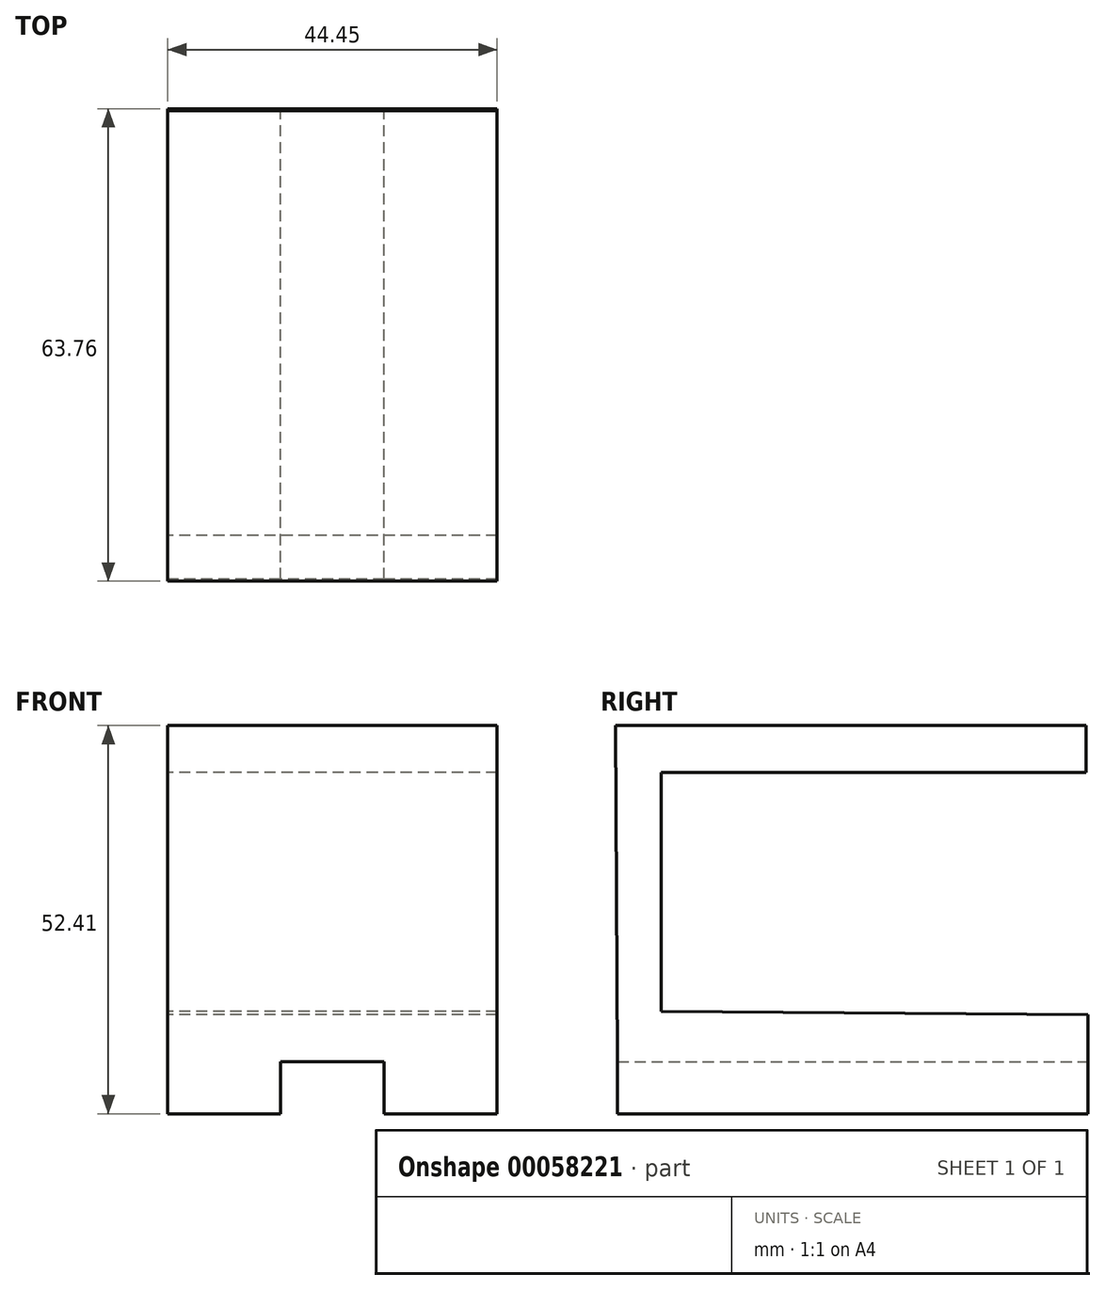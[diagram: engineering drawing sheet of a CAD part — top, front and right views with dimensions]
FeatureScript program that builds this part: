
annotation { "Feature Type Name" : "Feature", "Feature Type Description" : "" }
export const myFeature = defineFeature(function(context is Context, id is Id, definition is map)
    precondition{}
    {
        {
            var Q0;
            Q0=qCreatedBy(makeId("Right.planeOp"),FACE);
            var sketch = newSketch(context, id + "F0", { "sketchPlane" : qUnion([Q0])});
            skLineSegment(sketch, "E0.rect.bottom", {"start": v(31.75, -3.17) * mm, "end": v(-25.59, -3.17) * mm});
            skLineSegment(sketch, "E0.rect.top", {"start": v(31.75, 3.18) * mm, "end": v(-31.75, 3.18) * mm});
            skLineSegment(sketch, "E0.rect.left", {"start": v(31.75, -3.17) * mm, "end": v(31.75, 3.18) * mm});
            skPoint(sketch, "E0.rect.middle", {"position": v(0, 0) * mm});
            skLineSegment(sketch, "E1", {"start": v(-25.59, -3.17) * mm, "end": v(-25.59, -3.17) * mm});
            skLineSegment(sketch, "E2", {"start": v(-25.59, -3.17) * mm, "end": v(-25.59, -35.43) * mm});
            skLineSegment(sketch, "E3", {"start": v(-31.49, -42.23) * mm, "end": v(32.01, -42.23) * mm});
            skLineSegment(sketch, "E4", {"start": v(32.01, -42.23) * mm, "end": v(32.01, -35.88) * mm});
            skLineSegment(sketch, "E5", {"start": v(32.01, -35.88) * mm, "end": v(-25.59, -35.43) * mm});
            skLineSegment(sketch, "E6", {"start": v(-31.75, 3.17) * mm, "end": v(-31.49, -42.23) * mm});
            skSolve(sketch);
        }
        {
            var Q0;
            Q0 = qSketchRegion(id + "F0", true);
            extrude(context, id + "F1", {"entities" : qUnion([Q0]), "depth" : 44.45 * mm});
        }
        {
            var Q0;
            Q0=makeQuery(id+"F1.opExtrude","SWEPT_FACE",FACE,{"disambiguationData":[OSD([sQuery(id+"F0.wireOp",EDGE,"E3")])]});
            var sketch = newSketch(context, id + "F2", { "sketchPlane" : qUnion([Q0])});
            skLineSegment(sketch, "E7.bottom", {"start": v(44.45, 31.49) * mm, "end": v(29.23, 31.49) * mm});
            skLineSegment(sketch, "E7.top", {"start": v(44.45, -32.01) * mm, "end": v(29.23, -32.01) * mm});
            skLineSegment(sketch, "E7.left", {"start": v(44.45, 31.49) * mm, "end": v(44.45, -32.01) * mm});
            skLineSegment(sketch, "E7.right", {"start": v(29.23, 31.49) * mm, "end": v(29.23, -32.01) * mm});
            skLineSegment(sketch, "E8.bottom", {"start": v(0, 31.49) * mm, "end": v(15.23, 31.49) * mm});
            skLineSegment(sketch, "E8.top", {"start": v(0, -32.01) * mm, "end": v(15.23, -32.01) * mm});
            skLineSegment(sketch, "E8.left", {"start": v(0, 31.49) * mm, "end": v(0, -32.01) * mm});
            skLineSegment(sketch, "E8.right", {"start": v(15.23, 31.49) * mm, "end": v(15.23, -32.01) * mm});
            skLineSegment(sketch, "E9", {"start": v(29.23, 28.15) * mm, "end": v(15.23, 28.15) * mm, "construction": true});
            skLineSegment(sketch, "E10.bottom", {"start": v(29.23, 31.49) * mm, "end": v(15.23, 31.49) * mm, "construction": true});
            skLineSegment(sketch, "E10.top", {"start": v(29.23, -32.01) * mm, "end": v(15.23, -32.01) * mm, "construction": true});
            skLineSegment(sketch, "E10.left", {"start": v(29.23, 31.49) * mm, "end": v(29.23, -32.01) * mm, "construction": true});
            skLineSegment(sketch, "E10.right", {"start": v(15.23, 31.49) * mm, "end": v(15.23, -32.01) * mm, "construction": true});
            skLineSegment(sketch, "E11.bottom", {"start": v(29.23, 4.15) * mm, "end": v(15.23, 4.15) * mm, "construction": true});
            skLineSegment(sketch, "E11.top", {"start": v(29.23, -0.26) * mm, "end": v(15.23, -0.26) * mm, "construction": true});
            skLineSegment(sketch, "E11.left", {"start": v(29.23, 4.15) * mm, "end": v(29.23, -0.26) * mm, "construction": true});
            skLineSegment(sketch, "E11.right", {"start": v(15.23, 4.15) * mm, "end": v(15.23, -0.26) * mm, "construction": true});
            skSolve(sketch);
        }
        {
            var Q0;
            Q0 = qSketchRegion(id + "F2", true);
            extrude(context, id + "F3", {"entities" : qUnion([Q0]), "operationType" : NewBodyOperationType.ADD, "depth" : 7 * mm});
        }
    });
